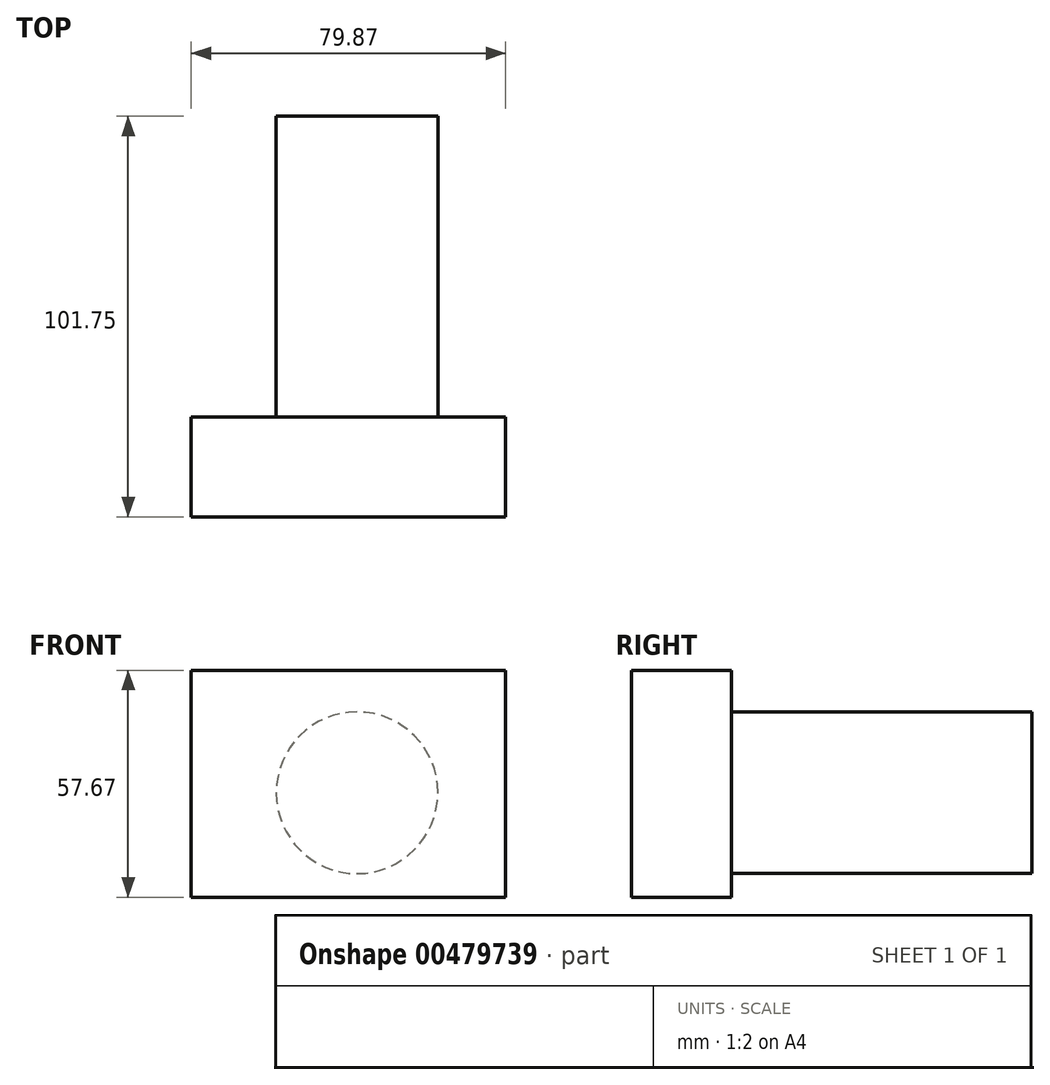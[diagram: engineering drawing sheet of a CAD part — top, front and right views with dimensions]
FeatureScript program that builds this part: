
annotation { "Feature Type Name" : "Feature", "Feature Type Description" : "" }
export const myFeature = defineFeature(function(context is Context, id is Id, definition is map)
    precondition{}
    {
        {
            var Q0;
            Q0=qCreatedBy(makeId("Front.planeOp"),FACE);
            var sketch = newSketch(context, id + "F0", { "sketchPlane" : qUnion([Q0])});
            skLineSegment(sketch, "E0", {"start": v(-42.11, 0) * mm, "end": v(-42.11, -57.67) * mm});
            skLineSegment(sketch, "E1", {"start": v(37.76, -57.67) * mm, "end": v(-42.11, -57.67) * mm});
            skLineSegment(sketch, "E2", {"start": v(37.76, -57.67) * mm, "end": v(37.76, 0) * mm});
            skLineSegment(sketch, "E3", {"start": v(37.76, 0) * mm, "end": v(-42.11, 0) * mm});
            skSolve(sketch);
        }
        {
            var Q0;
            Q0 = qSketchRegion(id + "F0", true);
            extrude(context, id + "F1", {"entities" : qUnion([Q0]), "depth" : 25.4 * mm});
        }
        {
            var Q0;
            Q0=makeQuery(id+"F1.opExtrude","CAP_FACE",FACE,{"disambiguationData":[OSD([sQuery(id+"F0.wireOp",EDGE,"E0"),sQuery(id+"F0.wireOp",EDGE,"E1"),sQuery(id+"F0.wireOp",EDGE,"E2"),sQuery(id+"F0.wireOp",EDGE,"E3")])],"isStart":false});
            var sketch = newSketch(context, id + "F2", { "sketchPlane" : qUnion([Q0])});
            skCircle(sketch, "E4", {"center": v(0, -31.12) * mm, "radius": 20.54 * mm});
            skSolve(sketch);
        }
        {
            var Q0;
            Q0 = qSketchRegion(id + "F2", true);
            extrude(context, id + "F3", {"entities" : qUnion([Q0]), "operationType" : NewBodyOperationType.ADD, "endBound" : BoundingType.THROUGH_ALL, "oppositeDirection" : true, "depth" : 25.4 * mm});
        }
    });
